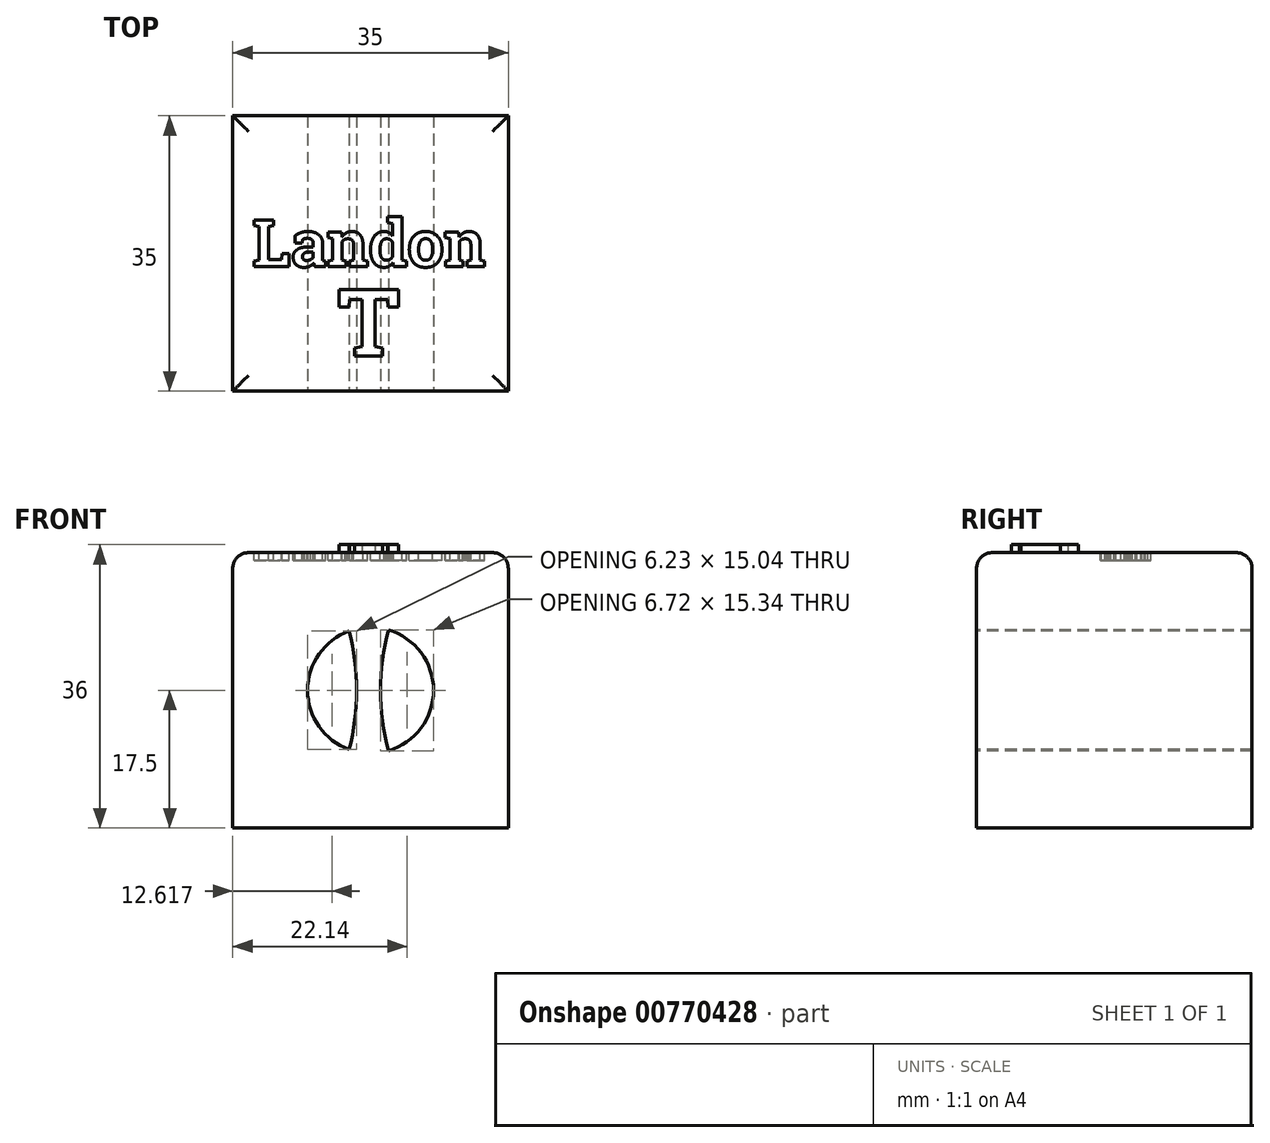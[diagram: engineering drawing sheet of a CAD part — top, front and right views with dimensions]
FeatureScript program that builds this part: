
annotation { "Feature Type Name" : "Feature", "Feature Type Description" : "" }
export const myFeature = defineFeature(function(context is Context, id is Id, definition is map)
    precondition{}
    {
        {
            var Q0;
            Q0=qCreatedBy(makeId("Top.planeOp"),FACE);
            var sketch = newSketch(context, id + "F0", { "sketchPlane" : qUnion([Q0])});
            skLineSegment(sketch, "E0.bottom", {"start": v(0, 0) * mm, "end": v(35, 0) * mm});
            skLineSegment(sketch, "E0.top", {"start": v(0, 35) * mm, "end": v(35, 35) * mm});
            skLineSegment(sketch, "E0.left", {"start": v(0, 0) * mm, "end": v(0, 35) * mm});
            skLineSegment(sketch, "E0.right", {"start": v(35, 0) * mm, "end": v(35, 35) * mm});
            skSolve(sketch);
        }
        {
            var Q0;
            Q0 = qSketchRegion(id + "F0", true);
            extrude(context, id + "F1", {"entities" : qUnion([Q0]), "depth" : 35 * mm, "offsetDistance" : 25 * mm});
        }
        {
            var Q0;
            Q0=makeQuery(id+"F1.opExtrude","CAP_FACE",FACE,{"disambiguationData":[OSD([sQuery(id+"F0.wireOp",EDGE,"E0.bottom"),sQuery(id+"F0.wireOp",EDGE,"E0.top"),sQuery(id+"F0.wireOp",EDGE,"E0.left"),sQuery(id+"F0.wireOp",EDGE,"E0.right")])],"isStart":false});
            var sketch = newSketch(context, id + "F2", { "sketchPlane" : qUnion([Q0])});
            skText(sketch, "E1", { "text": "Landon", "fontName": "RobotoSlab-Bold.ttf"});
            const initialGuessF2  = {"E1": [0.00248, 0.01581, 1, 0, 0.006]};
            skSetInitialGuess(sketch, initialGuessF2);
            skSolve(sketch);
        }
        {
            var Q0;
            Q0 = qSketchRegion(id + "F2", true);
            extrude(context, id + "F3", {"entities" : qUnion([Q0]), "operationType" : NewBodyOperationType.REMOVE, "oppositeDirection" : true, "depth" : 1 * mm, "offsetDistance" : 25 * mm});
        }
        {
            var Q0;
            Q0=makeQuery(id+"F1.opExtrude","CAP_EDGE",EDGE,{"disambiguationData":[OSD([sQuery(id+"F0.wireOp",EDGE,"E0.bottom")])],"isStart":false});
            var Q1;
            Q1=makeQuery(id+"F1.opExtrude","CAP_EDGE",EDGE,{"disambiguationData":[OSD([sQuery(id+"F0.wireOp",EDGE,"E0.left")])],"isStart":false});
            var Q2;
            Q2=makeQuery(id+"F1.opExtrude","CAP_EDGE",EDGE,{"disambiguationData":[OSD([sQuery(id+"F0.wireOp",EDGE,"E0.right")])],"isStart":false});
            var Q3;
            Q3=makeQuery(id+"F1.opExtrude","CAP_EDGE",EDGE,{"disambiguationData":[OSD([sQuery(id+"F0.wireOp",EDGE,"E0.top")])],"isStart":false});
            fillet(context, id + "F4", {"entities" : qUnion([Q0, Q1, Q2, Q3]), "tangentPropagation" : true, "radius" : 2 * mm, "defaultsChanged" : true, "vertexSettings" : [], "allowEdgeOverflow" : false});
        }
        {
            var Q0;
            {var subQ0=sQuery(id+"F0.wireOp",EDGE,"E0.top");var subQ1=sQuery(id+"F0.wireOp",EDGE,"E0.right");var subQ2=sQuery(id+"F0.wireOp",EDGE,"E0.bottom");var subQ3=sQuery(id+"F0.wireOp",EDGE,"E0.left");Q0=makeQuery(id+"F3.boolean.opBoolean","SPLIT",FACE,{"disambiguationData":[TD([makeQuery(id+"F1.opExtrude","SWEPT_FACE",FACE,{"disambiguationData":[OSD([subQ2])]})])],"derivedFrom":makeQuery(id+"F1.opExtrude","CAP_FACE",FACE,{"disambiguationData":[OSD([subQ2,subQ0,subQ3,subQ1])],"isStart":false})});}
            var sketch = newSketch(context, id + "F5", { "sketchPlane" : qUnion([Q0])});
            skText(sketch, "E2", { "text": "T", "fontName": "RobotoSlab-Bold.ttf"});
            const initialGuessF5  = {"E2": [0.01325, 0.00446, 1, 0, 0.00857]};
            skSetInitialGuess(sketch, initialGuessF5);
            skSolve(sketch);
        }
        {
            var Q0;
            Q0 = qSketchRegion(id + "F5", true);
            extrude(context, id + "F6", {"entities" : qUnion([Q0]), "operationType" : NewBodyOperationType.ADD, "depth" : 1 * mm, "offsetDistance" : 25 * mm});
        }
        {
            var Q0;
            Q0=makeQuery(id+"F1.opExtrude","SWEPT_FACE",FACE,{"disambiguationData":[OSD([sQuery(id+"F0.wireOp",EDGE,"E0.bottom")])]});
            var sketch = newSketch(context, id + "F7", { "sketchPlane" : qUnion([Q0])});
            skCircle(sketch, "E3", {"center": v(17.5, 17.5) * mm, "radius": 8 * mm});
            skSolve(sketch);
        }
        {
            var Q0;
            Q0 = qSketchRegion(id + "F7", true);
            extrude(context, id + "F8", {"entities" : qUnion([Q0]), "operationType" : NewBodyOperationType.REMOVE, "endBound" : BoundingType.THROUGH_ALL, "oppositeDirection" : true, "depth" : 25 * mm, "offsetDistance" : 25 * mm});
        }
        {
            var Q0;
            Q0=makeQuery(id+"F1.opExtrude","SWEPT_FACE",FACE,{"disambiguationData":[OSD([sQuery(id+"F0.wireOp",EDGE,"E0.bottom")])]});
            var sketch = newSketch(context, id + "F9", { "sketchPlane" : qUnion([Q0])});
            skArc(sketch, "E4", {"start": v(14.78, 9.98) * mm, "mid": v(15.73, 17.5) * mm, "end": v(14.78, 25.02) * mm});
            skArc(sketch, "E5", {"start": v(19.78, 25.17) * mm, "mid": v(18.78, 17.5) * mm, "end": v(19.78, 9.83) * mm});
            skArc(sketch, "E6", {"start": v(14.78, 9.98) * mm, "mid": v(17.26, 9.5) * mm, "end": v(19.78, 9.83) * mm});
            skArc(sketch, "E7.trimOffspring", {"start": v(19.78, 25.17) * mm, "mid": v(17.26, 25.5) * mm, "end": v(14.78, 25.02) * mm});
            skSolve(sketch);
        }
        {
            var Q0;
            Q0 = qSketchRegion(id + "F9", true);
            var Q1;
            Q1=makeQuery(id+"F1.opExtrude","SWEPT_FACE",FACE,{"disambiguationData":[OSD([sQuery(id+"F0.wireOp",EDGE,"E0.top")])]});
            extrude(context, id + "F10", {"entities" : qUnion([Q0]), "operationType" : NewBodyOperationType.ADD, "endBound" : BoundingType.UP_TO_SURFACE, "oppositeDirection" : true, "depth" : 25 * mm, "endBoundEntityFace" : qUnion([Q1]), "offsetDistance" : 25 * mm});
        }
    });
